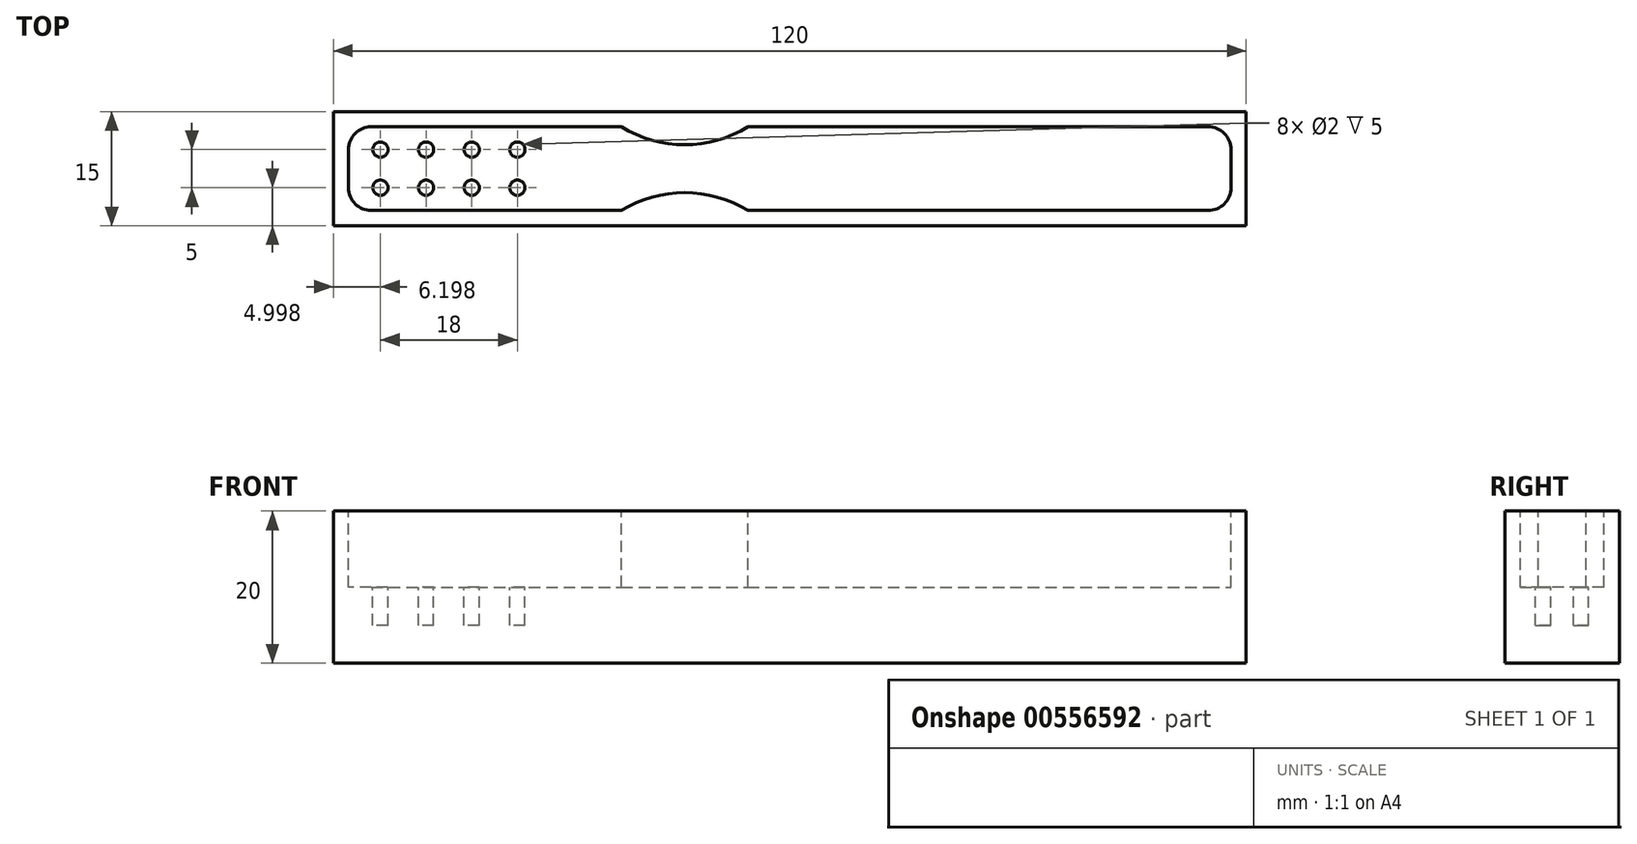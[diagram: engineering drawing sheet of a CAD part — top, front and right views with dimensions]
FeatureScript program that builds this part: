
annotation { "Feature Type Name" : "Feature", "Feature Type Description" : "" }
export const myFeature = defineFeature(function(context is Context, id is Id, definition is map)
    precondition{}
    {
        {
            var Q0;
            Q0=qCreatedBy(makeId("Top.planeOp"),FACE);
            var sketch = newSketch(context, id + "F0", { "sketchPlane" : qUnion([Q0])});
            skLineSegment(sketch, "E0.bottom", {"start": v(-13, 1.28) * mm, "end": v(107, 1.28) * mm});
            skLineSegment(sketch, "E0.top", {"start": v(-13, -13.72) * mm, "end": v(107, -13.72) * mm});
            skLineSegment(sketch, "E0.left", {"start": v(-13, 1.28) * mm, "end": v(-13, -13.72) * mm});
            skLineSegment(sketch, "E0.right", {"start": v(107, 1.28) * mm, "end": v(107, -13.72) * mm});
            skSolve(sketch);
        }
        {
            var Q0;
            Q0 = qSketchRegion(id + "F0", true);
            extrude(context, id + "F1", {"entities" : qUnion([Q0]), "depth" : 20 * mm, "offsetDistance" : 25.4 * mm});
        }
        {
            var Q0;
            Q0=makeQuery(id+"F1.opExtrude","CAP_FACE",FACE,{"disambiguationData":[OSD([sQuery(id+"F0.wireOp",EDGE,"E0.bottom"),sQuery(id+"F0.wireOp",EDGE,"E0.top"),sQuery(id+"F0.wireOp",EDGE,"E0.left"),sQuery(id+"F0.wireOp",EDGE,"E0.right")])],"isStart":false});
            var sketch = newSketch(context, id + "F2", { "sketchPlane" : qUnion([Q0])});
            skLineSegment(sketch, "E1.bottom", {"start": v(-8, -0.72) * mm, "end": v(24.87, -0.72) * mm});
            skLineSegment(sketch, "E1.top", {"start": v(-8, -11.72) * mm, "end": v(24.87, -11.72) * mm});
            skLineSegment(sketch, "E1.left", {"start": v(-11, -3.72) * mm, "end": v(-11, -8.72) * mm});
            skLineSegment(sketch, "E1.right", {"start": v(105, -3.72) * mm, "end": v(105, -8.72) * mm});
            skPoint(sketch, "E2.visualSharp", {"position": v(-11, -0.72) * mm});
            skArc(sketch, "E2.filletArc", {"start": v(-8, -0.72) * mm, "mid": v(-10.12, -1.6) * mm, "end": v(-11, -3.72) * mm});
            skPoint(sketch, "E3.visualSharp", {"position": v(-11, -11.72) * mm});
            skArc(sketch, "E3.filletArc", {"start": v(-11, -8.72) * mm, "mid": v(-10.12, -10.84) * mm, "end": v(-8, -11.72) * mm});
            skPoint(sketch, "E4.visualSharp", {"position": v(105, -11.72) * mm});
            skArc(sketch, "E4.filletArc", {"start": v(102, -11.72) * mm, "mid": v(104.13, -10.84) * mm, "end": v(105, -8.72) * mm});
            skPoint(sketch, "E5.visualSharp", {"position": v(105, -0.72) * mm});
            skArc(sketch, "E5.filletArc", {"start": v(105, -3.72) * mm, "mid": v(104.13, -1.6) * mm, "end": v(102, -0.72) * mm});
            skArc(sketch, "E6", {"start": v(24.87, -0.72) * mm, "mid": v(33.19, -3.07) * mm, "end": v(41.5, -0.72) * mm});
            skLineSegment(sketch, "E7", {"start": v(105, -6.22) * mm, "end": v(-11, -6.22) * mm});
            skArc(sketch, "E8.MirrorCS", {"start": v(24.87, -11.72) * mm, "mid": v(33.19, -9.38) * mm, "end": v(41.5, -11.72) * mm});
            skLineSegment(sketch, "E9", {"start": v(24.87, -11.72) * mm, "end": v(41.5, -11.72) * mm});
            skLineSegment(sketch, "E10", {"start": v(41.5, -11.72) * mm, "end": v(41.5, -11.72) * mm});
            skLineSegment(sketch, "E11", {"start": v(41.5, -0.72) * mm, "end": v(102, -0.72) * mm});
            skLineSegment(sketch, "E12", {"start": v(24.87, -0.72) * mm, "end": v(41.5, -0.72) * mm});
            skLineSegment(sketch, "E13", {"start": v(41.5, -11.72) * mm, "end": v(102, -11.72) * mm});
            skSolve(sketch);
        }
        {
            var Q0;
            Q0=makeQuery(id+"F2.imprint","IMPRINT",FACE,{"disambiguationData":[TD([[makeQuery(id+"F2.imprint","IMPRINT",EDGE,{"derivedFrom":sQuery(id+"F2.wireOp",EDGE,"E1.bottom")}),-1.0]])]});
            var Q1;
            Q1=makeQuery(id+"F2.imprint","IMPRINT",FACE,{"disambiguationData":[TD([[makeQuery(id+"F2.imprint","IMPRINT",EDGE,{"derivedFrom":sQuery(id+"F2.wireOp",EDGE,"E1.top")}),1.0]])]});
            extrude(context, id + "F3", {"entities" : qUnion([Q0, Q1]), "operationType" : NewBodyOperationType.REMOVE, "oppositeDirection" : true, "depth" : 10 * mm, "offsetDistance" : 25.4 * mm});
        }
        {
            var Q0;
            Q0=makeQuery(id+"F3.boolean.opBoolean","COPY",FACE,{"derivedFrom":makeQuery(id+"F3.opExtrude","CAP_FACE",FACE,{"disambiguationData":[OSD([sQuery(id+"F2.wireOp",EDGE,"E1.bottom"),sQuery(id+"F2.wireOp",EDGE,"E1.top"),sQuery(id+"F2.wireOp",EDGE,"E1.left"),sQuery(id+"F2.wireOp",EDGE,"E1.right"),sQuery(id+"F2.wireOp",EDGE,"E2.filletArc"),sQuery(id+"F2.wireOp",EDGE,"E3.filletArc"),sQuery(id+"F2.wireOp",EDGE,"E4.filletArc"),sQuery(id+"F2.wireOp",EDGE,"E5.filletArc")])],"isStart":false})});
            var sketch = newSketch(context, id + "F4", { "sketchPlane" : qUnion([Q0])});
            skCircle(sketch, "E14", {"center": v(-6.8, -3.72) * mm, "radius": 1 * mm});
            skCircle(sketch, "E15.1.0.0", {"center": v(-0.8, -3.72) * mm, "radius": 1 * mm});
            skCircle(sketch, "E15.2.0.0", {"center": v(5.2, -3.72) * mm, "radius": 1 * mm});
            skCircle(sketch, "E15.3.0.0", {"center": v(11.2, -3.72) * mm, "radius": 1 * mm});
            skLineSegment(sketch, "E15.direction1", {"start": v(-6.8, -3.72) * mm, "end": v(-0.8, -3.72) * mm, "construction": true});
            skCircle(sketch, "E16.0.1.0", {"center": v(-6.8, -8.72) * mm, "radius": 1 * mm});
            skCircle(sketch, "E16.0.1.1", {"center": v(-0.8, -8.72) * mm, "radius": 1 * mm});
            skCircle(sketch, "E16.0.1.2", {"center": v(5.2, -8.72) * mm, "radius": 1 * mm});
            skCircle(sketch, "E16.0.1.3", {"center": v(11.2, -8.72) * mm, "radius": 1 * mm});
            skLineSegment(sketch, "E16.direction1", {"start": v(-6.8, -3.72) * mm, "end": v(18.6, -3.72) * mm, "construction": true});
            skLineSegment(sketch, "E16.direction2", {"start": v(-6.8, -3.72) * mm, "end": v(-6.8, -8.72) * mm, "construction": true});
            skSolve(sketch);
        }
        {
            var Q0;
            Q0=makeQuery(id+"F4.imprint","IMPRINT",FACE,{"disambiguationData":[TD([[makeQuery(id+"F4.imprint","IMPRINT",EDGE,{"derivedFrom":sQuery(id+"F4.wireOp",EDGE,"E14")}),1.0]])]});
            var Q1;
            Q1=makeQuery(id+"F4.imprint","IMPRINT",FACE,{"disambiguationData":[TD([[makeQuery(id+"F4.imprint","IMPRINT",EDGE,{"derivedFrom":sQuery(id+"F4.wireOp",EDGE,"E15.1.0.0")}),1.0]])]});
            var Q2;
            Q2=makeQuery(id+"F4.imprint","IMPRINT",FACE,{"disambiguationData":[TD([[makeQuery(id+"F4.imprint","IMPRINT",EDGE,{"derivedFrom":sQuery(id+"F4.wireOp",EDGE,"E15.2.0.0")}),1.0]])]});
            var Q3;
            Q3=makeQuery(id+"F4.imprint","IMPRINT",FACE,{"disambiguationData":[TD([[makeQuery(id+"F4.imprint","IMPRINT",EDGE,{"derivedFrom":sQuery(id+"F4.wireOp",EDGE,"E15.3.0.0")}),1.0]])]});
            var Q4;
            Q4=makeQuery(id+"F4.imprint","IMPRINT",FACE,{"disambiguationData":[TD([[makeQuery(id+"F4.imprint","IMPRINT",EDGE,{"derivedFrom":sQuery(id+"F4.wireOp",EDGE,"E16.0.1.3")}),1.0]])]});
            var Q5;
            Q5=makeQuery(id+"F4.imprint","IMPRINT",FACE,{"disambiguationData":[TD([[makeQuery(id+"F4.imprint","IMPRINT",EDGE,{"derivedFrom":sQuery(id+"F4.wireOp",EDGE,"E16.0.1.2")}),1.0]])]});
            var Q6;
            Q6=makeQuery(id+"F4.imprint","IMPRINT",FACE,{"disambiguationData":[TD([[makeQuery(id+"F4.imprint","IMPRINT",EDGE,{"derivedFrom":sQuery(id+"F4.wireOp",EDGE,"E16.0.1.1")}),1.0]])]});
            var Q7;
            Q7=makeQuery(id+"F4.imprint","IMPRINT",FACE,{"disambiguationData":[TD([[makeQuery(id+"F4.imprint","IMPRINT",EDGE,{"derivedFrom":sQuery(id+"F4.wireOp",EDGE,"E16.0.1.0")}),1.0]])]});
            extrude(context, id + "F5", {"entities" : qUnion([Q0, Q1, Q2, Q3, Q4, Q5, Q6, Q7]), "operationType" : NewBodyOperationType.REMOVE, "oppositeDirection" : true, "depth" : 5 * mm, "offsetDistance" : 25.4 * mm});
        }
    });
